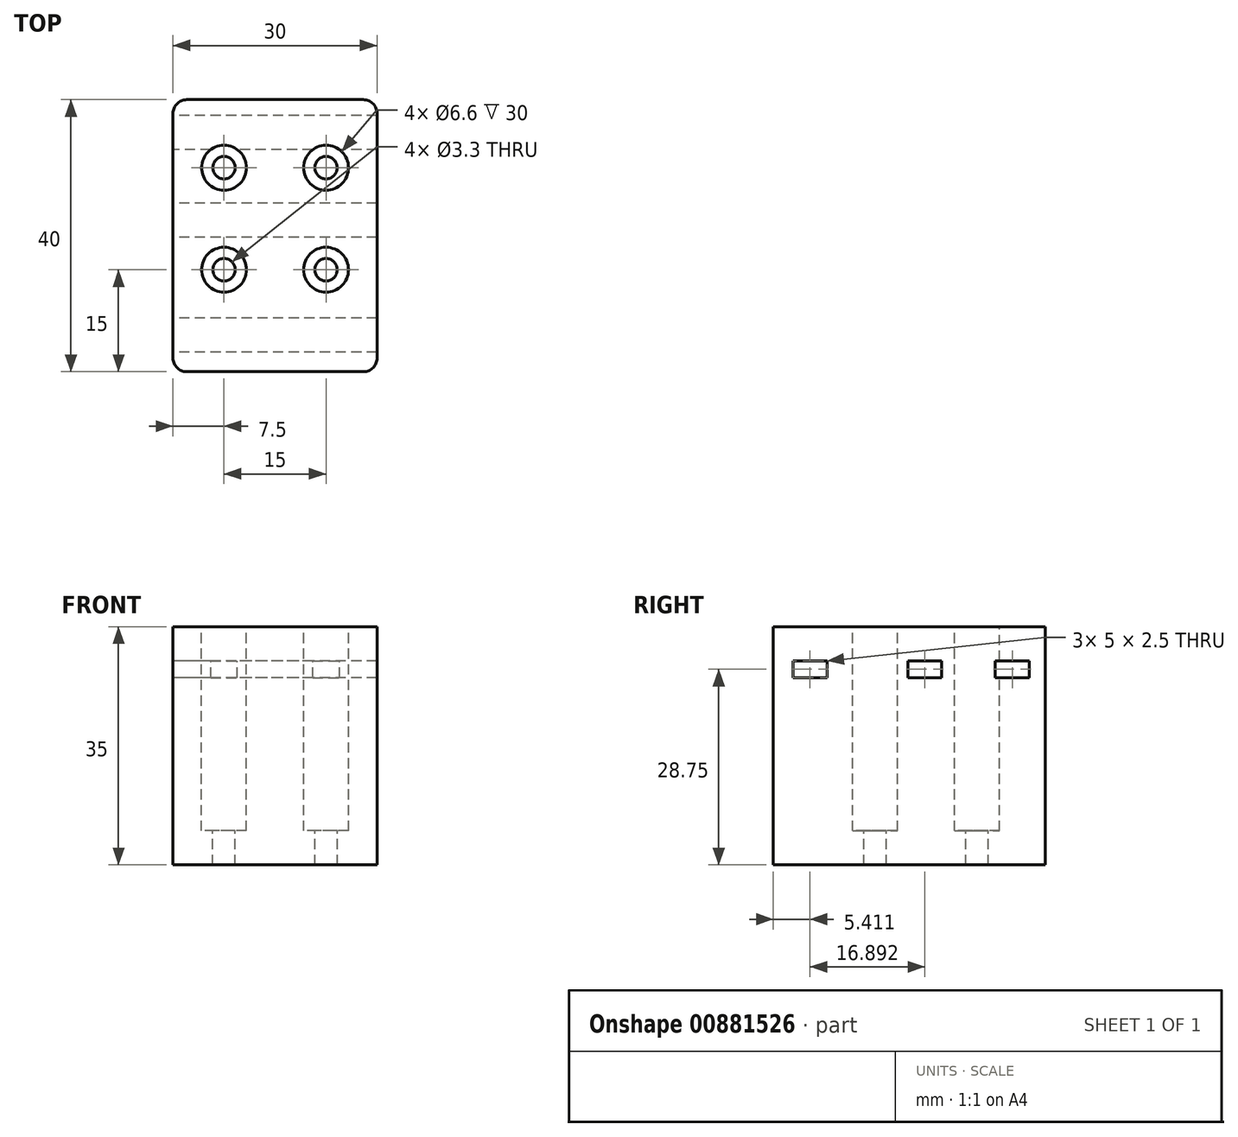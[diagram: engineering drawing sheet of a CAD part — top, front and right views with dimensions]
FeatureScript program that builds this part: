
annotation { "Feature Type Name" : "Feature", "Feature Type Description" : "" }
export const myFeature = defineFeature(function(context is Context, id is Id, definition is map)
    precondition{}
    {
        {
            var Q0;
            Q0=qCreatedBy(makeId("Top.planeOp"),FACE);
            var sketch = newSketch(context, id + "F0", { "sketchPlane" : qUnion([Q0])});
            skLineSegment(sketch, "E0.bottom", {"start": v(0, 0) * mm, "end": v(30, 0) * mm});
            skLineSegment(sketch, "E0.top", {"start": v(0, -40) * mm, "end": v(30, -40) * mm});
            skLineSegment(sketch, "E0.left", {"start": v(0, 0) * mm, "end": v(0, -40) * mm});
            skLineSegment(sketch, "E0.right", {"start": v(30, 0) * mm, "end": v(30, -40) * mm});
            skSolve(sketch);
        }
        {
            var Q0;
            Q0=makeQuery(id+"F0.imprint","IMPRINT",FACE,{"disambiguationData":[TD([[makeQuery(id+"F0.imprint","IMPRINT",EDGE,{"derivedFrom":sQuery(id+"F0.wireOp",EDGE,"E0.bottom")}),-1.0]])]});
            extrude(context, id + "F1", {"entities" : qUnion([Q0]), "depth" : 35 * mm, "offsetDistance" : 25 * mm});
        }
        {
            var Q0;
            Q0=makeQuery(id+"F1.opExtrude","CAP_FACE",FACE,{"disambiguationData":[OSD([sQuery(id+"F0.wireOp",EDGE,"E0.bottom"),sQuery(id+"F0.wireOp",EDGE,"E0.top"),sQuery(id+"F0.wireOp",EDGE,"E0.left"),sQuery(id+"F0.wireOp",EDGE,"E0.right")])],"isStart":false});
            var sketch = newSketch(context, id + "F2", { "sketchPlane" : qUnion([Q0])});
            skCircle(sketch, "E1", {"center": v(7.5, -10) * mm, "radius": 3.3 * mm});
            skCircle(sketch, "E2", {"center": v(22.5, -10) * mm, "radius": 3.3 * mm});
            skCircle(sketch, "E3", {"center": v(7.5, -25) * mm, "radius": 3.3 * mm});
            skCircle(sketch, "E4", {"center": v(22.5, -25) * mm, "radius": 3.3 * mm});
            skSolve(sketch);
        }
        {
            var Q0;
            Q0=makeQuery(id+"F2.imprint","IMPRINT",FACE,{"disambiguationData":[TD([[makeQuery(id+"F2.imprint","IMPRINT",EDGE,{"derivedFrom":sQuery(id+"F2.wireOp",EDGE,"E1")}),1.0]])]});
            var Q1;
            Q1=makeQuery(id+"F2.imprint","IMPRINT",FACE,{"disambiguationData":[TD([[makeQuery(id+"F2.imprint","IMPRINT",EDGE,{"derivedFrom":sQuery(id+"F2.wireOp",EDGE,"E2")}),1.0]])]});
            var Q2;
            Q2=makeQuery(id+"F2.imprint","IMPRINT",FACE,{"disambiguationData":[TD([[makeQuery(id+"F2.imprint","IMPRINT",EDGE,{"derivedFrom":sQuery(id+"F2.wireOp",EDGE,"E3")}),1.0]])]});
            var Q3;
            Q3=makeQuery(id+"F2.imprint","IMPRINT",FACE,{"disambiguationData":[TD([[makeQuery(id+"F2.imprint","IMPRINT",EDGE,{"derivedFrom":sQuery(id+"F2.wireOp",EDGE,"E4")}),1.0]])]});
            extrude(context, id + "F3", {"entities" : qUnion([Q0, Q1, Q2, Q3]), "operationType" : NewBodyOperationType.REMOVE, "oppositeDirection" : true, "depth" : 30 * mm, "offsetDistance" : 25 * mm});
        }
        {
            var Q0;
            Q0=makeQuery(id+"F1.opExtrude","SWEPT_FACE",FACE,{"disambiguationData":[OSD([sQuery(id+"F0.wireOp",EDGE,"E0.left")])]});
            var sketch = newSketch(context, id + "F4", { "sketchPlane" : qUnion([Q0])});
            skLineSegment(sketch, "E5.bottom", {"start": v(2.35, 30) * mm, "end": v(7.35, 30) * mm});
            skLineSegment(sketch, "E5.top", {"start": v(2.35, 27.5) * mm, "end": v(7.35, 27.5) * mm});
            skLineSegment(sketch, "E5.left", {"start": v(2.35, 30) * mm, "end": v(2.35, 27.5) * mm});
            skLineSegment(sketch, "E5.right", {"start": v(7.35, 30) * mm, "end": v(7.35, 27.5) * mm});
            skLineSegment(sketch, "E6.bottom", {"start": v(15.2, 27.5) * mm, "end": v(20.2, 27.5) * mm});
            skLineSegment(sketch, "E6.top", {"start": v(15.2, 30) * mm, "end": v(20.2, 30) * mm});
            skLineSegment(sketch, "E6.left", {"start": v(15.2, 27.5) * mm, "end": v(15.2, 30) * mm});
            skLineSegment(sketch, "E6.right", {"start": v(20.2, 27.5) * mm, "end": v(20.2, 30) * mm});
            skLineSegment(sketch, "E7.bottom", {"start": v(32.09, 27.5) * mm, "end": v(37.09, 27.5) * mm});
            skLineSegment(sketch, "E7.top", {"start": v(32.09, 30) * mm, "end": v(37.09, 30) * mm});
            skLineSegment(sketch, "E7.left", {"start": v(32.09, 27.5) * mm, "end": v(32.09, 30) * mm});
            skLineSegment(sketch, "E7.right", {"start": v(37.09, 27.5) * mm, "end": v(37.09, 30) * mm});
            skSolve(sketch);
        }
        {
            var Q0;
            Q0=makeQuery(id+"F4.imprint","IMPRINT",FACE,{"disambiguationData":[TD([[makeQuery(id+"F4.imprint","IMPRINT",EDGE,{"derivedFrom":sQuery(id+"F4.wireOp",EDGE,"E5.bottom")}),-1.0]])]});
            var Q1;
            Q1=makeQuery(id+"F4.imprint","IMPRINT",FACE,{"disambiguationData":[TD([[makeQuery(id+"F4.imprint","IMPRINT",EDGE,{"derivedFrom":sQuery(id+"F4.wireOp",EDGE,"E6.bottom")}),1.0]])]});
            var Q2;
            Q2=makeQuery(id+"F4.imprint","IMPRINT",FACE,{"disambiguationData":[TD([[makeQuery(id+"F4.imprint","IMPRINT",EDGE,{"derivedFrom":sQuery(id+"F4.wireOp",EDGE,"E7.bottom")}),1.0]])]});
            extrude(context, id + "F5", {"entities" : qUnion([Q0, Q1, Q2]), "operationType" : NewBodyOperationType.REMOVE, "endBound" : BoundingType.THROUGH_ALL, "oppositeDirection" : true, "depth" : 25 * mm, "offsetDistance" : 25 * mm});
        }
        {
            var Q0;
            Q0=makeQuery(id+"F3.boolean.opBoolean","COPY",FACE,{"derivedFrom":makeQuery(id+"F3.opExtrude","CAP_FACE",FACE,{"disambiguationData":[OSD([sQuery(id+"F2.wireOp",EDGE,"E1")])],"isStart":false})});
            var sketch = newSketch(context, id + "F6", { "sketchPlane" : qUnion([Q0])});
            skCircle(sketch, "E8", {"center": v(7.5, -10) * mm, "radius": 1.65 * mm});
            skSolve(sketch);
        }
        {
            var Q0;
            Q0=makeQuery(id+"F6.imprint","IMPRINT",FACE,{"disambiguationData":[TD([[makeQuery(id+"F6.imprint","IMPRINT",EDGE,{"derivedFrom":sQuery(id+"F6.wireOp",EDGE,"E8")}),1.0]])]});
            extrude(context, id + "F7", {"entities" : qUnion([Q0]), "operationType" : NewBodyOperationType.REMOVE, "endBound" : BoundingType.THROUGH_ALL, "oppositeDirection" : true, "depth" : 25 * mm, "offsetDistance" : 25 * mm});
        }
        {
            var Q0;
            Q0=makeQuery(id+"F3.boolean.opBoolean","COPY",FACE,{"derivedFrom":makeQuery(id+"F3.opExtrude","CAP_FACE",FACE,{"disambiguationData":[OSD([sQuery(id+"F2.wireOp",EDGE,"E3")])],"isStart":false})});
            var sketch = newSketch(context, id + "F8", { "sketchPlane" : qUnion([Q0])});
            skCircle(sketch, "E9", {"center": v(7.5, -25) * mm, "radius": 1.65 * mm});
            skSolve(sketch);
        }
        {
            var Q0;
            Q0=makeQuery(id+"F8.imprint","IMPRINT",FACE,{"disambiguationData":[TD([[makeQuery(id+"F8.imprint","IMPRINT",EDGE,{"derivedFrom":sQuery(id+"F8.wireOp",EDGE,"E9")}),1.0]])]});
            extrude(context, id + "F9", {"entities" : qUnion([Q0]), "operationType" : NewBodyOperationType.REMOVE, "endBound" : BoundingType.THROUGH_ALL, "oppositeDirection" : true, "depth" : 25 * mm, "offsetDistance" : 25 * mm});
        }
        {
            var Q0;
            Q0=makeQuery(id+"F3.boolean.opBoolean","COPY",FACE,{"derivedFrom":makeQuery(id+"F3.opExtrude","CAP_FACE",FACE,{"disambiguationData":[OSD([sQuery(id+"F2.wireOp",EDGE,"E4")])],"isStart":false})});
            var sketch = newSketch(context, id + "F10", { "sketchPlane" : qUnion([Q0])});
            skCircle(sketch, "E10", {"center": v(22.5, -25) * mm, "radius": 1.65 * mm});
            skSolve(sketch);
        }
        {
            var Q0;
            Q0=makeQuery(id+"F10.imprint","IMPRINT",FACE,{"disambiguationData":[TD([[makeQuery(id+"F10.imprint","IMPRINT",EDGE,{"derivedFrom":sQuery(id+"F10.wireOp",EDGE,"E10")}),1.0]])]});
            extrude(context, id + "F11", {"entities" : qUnion([Q0]), "operationType" : NewBodyOperationType.REMOVE, "endBound" : BoundingType.THROUGH_ALL, "oppositeDirection" : true, "depth" : 25 * mm, "offsetDistance" : 25 * mm});
        }
        {
            var Q0;
            Q0=makeQuery(id+"F3.boolean.opBoolean","COPY",FACE,{"derivedFrom":makeQuery(id+"F3.opExtrude","CAP_FACE",FACE,{"disambiguationData":[OSD([sQuery(id+"F2.wireOp",EDGE,"E2")])],"isStart":false})});
            var sketch = newSketch(context, id + "F12", { "sketchPlane" : qUnion([Q0])});
            skCircle(sketch, "E11", {"center": v(22.5, -10) * mm, "radius": 1.65 * mm});
            skSolve(sketch);
        }
        {
            var Q0;
            Q0=makeQuery(id+"F12.imprint","IMPRINT",FACE,{"disambiguationData":[TD([[makeQuery(id+"F12.imprint","IMPRINT",EDGE,{"derivedFrom":sQuery(id+"F12.wireOp",EDGE,"E11")}),1.0]])]});
            extrude(context, id + "F13", {"entities" : qUnion([Q0]), "operationType" : NewBodyOperationType.REMOVE, "endBound" : BoundingType.THROUGH_ALL, "oppositeDirection" : true, "depth" : 25 * mm, "offsetDistance" : 25 * mm});
        }
        {
            var Q0;
            Q0=makeQuery(id+"F1.opExtrude","SWEPT_EDGE",EDGE,{"disambiguationData":[OSD([sQuery(id+"F0.wireOp",EDGE,"E0.bottom"),sQuery(id+"F0.wireOp",EDGE,"E0.left")])]});
            var Q1;
            Q1=makeQuery(id+"F1.opExtrude","SWEPT_EDGE",EDGE,{"disambiguationData":[OSD([sQuery(id+"F0.wireOp",EDGE,"E0.bottom"),sQuery(id+"F0.wireOp",EDGE,"E0.right")])]});
            var Q2;
            Q2=makeQuery(id+"F1.opExtrude","SWEPT_EDGE",EDGE,{"disambiguationData":[OSD([sQuery(id+"F0.wireOp",EDGE,"E0.top"),sQuery(id+"F0.wireOp",EDGE,"E0.right")])]});
            var Q3;
            Q3=makeQuery(id+"F1.opExtrude","SWEPT_EDGE",EDGE,{"disambiguationData":[OSD([sQuery(id+"F0.wireOp",EDGE,"E0.top"),sQuery(id+"F0.wireOp",EDGE,"E0.left")])]});
            fillet(context, id + "F14", {"entities" : qUnion([Q0, Q1, Q2, Q3]), "radius" : 2 * mm, "tangentPropagation" : true, "allowEdgeOverflow" : false});
        }
    });
